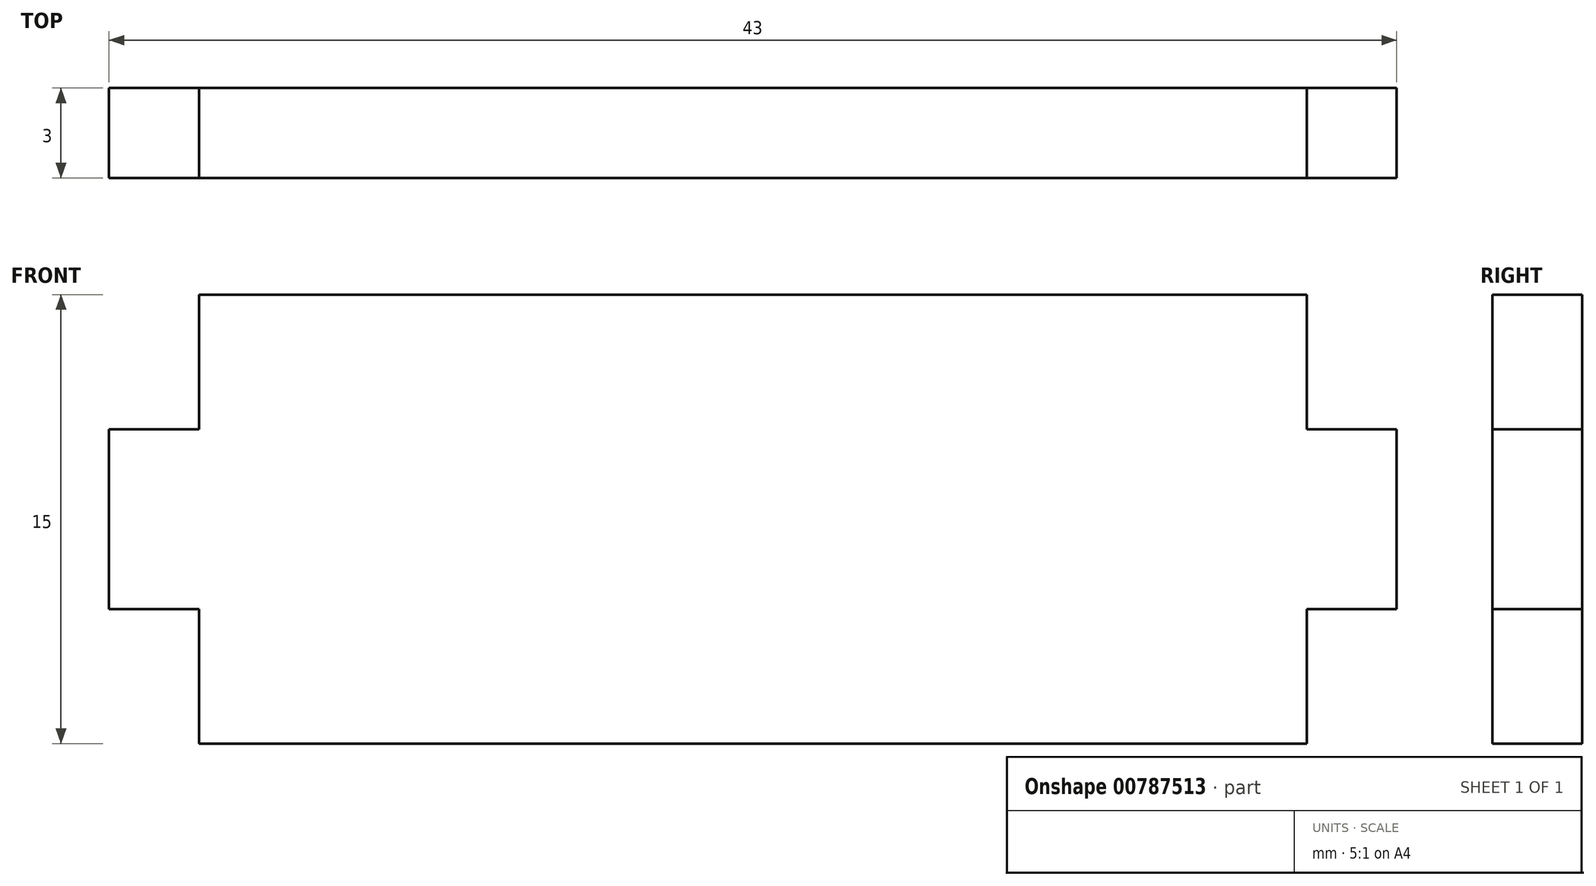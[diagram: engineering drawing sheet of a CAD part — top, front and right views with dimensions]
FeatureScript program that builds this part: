
annotation { "Feature Type Name" : "Feature", "Feature Type Description" : "" }
export const myFeature = defineFeature(function(context is Context, id is Id, definition is map)
    precondition{}
    {
        {
            var Q0;
            Q0=qCreatedBy(makeId("Front.planeOp"),FACE);
            var sketch = newSketch(context, id + "F0", { "sketchPlane" : qUnion([Q0])});
            skLineSegment(sketch, "E0", {"start": v(-17.95, 16.69) * mm, "end": v(19.05, 16.69) * mm});
            skLineSegment(sketch, "E1", {"start": v(19.05, 16.69) * mm, "end": v(19.05, 12.19) * mm});
            skLineSegment(sketch, "E2", {"start": v(19.05, 12.19) * mm, "end": v(22.05, 12.19) * mm});
            skLineSegment(sketch, "E3", {"start": v(22.05, 12.19) * mm, "end": v(22.05, 6.19) * mm});
            skLineSegment(sketch, "E4", {"start": v(22.05, 6.19) * mm, "end": v(19.05, 6.19) * mm});
            skLineSegment(sketch, "E5", {"start": v(19.05, 6.19) * mm, "end": v(19.05, 1.69) * mm});
            skLineSegment(sketch, "E6", {"start": v(19.05, 1.69) * mm, "end": v(-17.95, 1.69) * mm});
            skLineSegment(sketch, "E7", {"start": v(-17.95, 1.69) * mm, "end": v(-17.95, 6.19) * mm});
            skLineSegment(sketch, "E8", {"start": v(-17.95, 6.19) * mm, "end": v(-20.95, 6.19) * mm});
            skLineSegment(sketch, "E9", {"start": v(-20.95, 6.19) * mm, "end": v(-20.95, 12.19) * mm});
            skLineSegment(sketch, "E10", {"start": v(-20.95, 12.19) * mm, "end": v(-17.95, 12.19) * mm});
            skLineSegment(sketch, "E11", {"start": v(-17.95, 12.19) * mm, "end": v(-17.95, 16.69) * mm});
            skPoint(sketch, "E12", {"position": v(-19.45, 12.19) * mm});
            skPoint(sketch, "E13", {"position": v(20.55, 12.19) * mm});
            skPoint(sketch, "E14", {"position": v(22.05, 9.19) * mm});
            skLineSegment(sketch, "E15", {"start": v(0.55, 16.69) * mm, "end": v(0.55, 1.69) * mm, "construction": true});
            skSolve(sketch);
        }
        {
            var Q0;
            Q0=makeQuery(id+"F0.imprint","IMPRINT",FACE,{"disambiguationData":[TD([[makeQuery(id+"F0.imprint","IMPRINT",EDGE,{"derivedFrom":sQuery(id+"F0.wireOp",EDGE,"E0")}),-1.0]])]});
            extrude(context, id + "F1", {"entities" : qUnion([Q0]), "depth" : 3 * mm, "offsetDistance" : 25.4 * mm});
        }
    });
